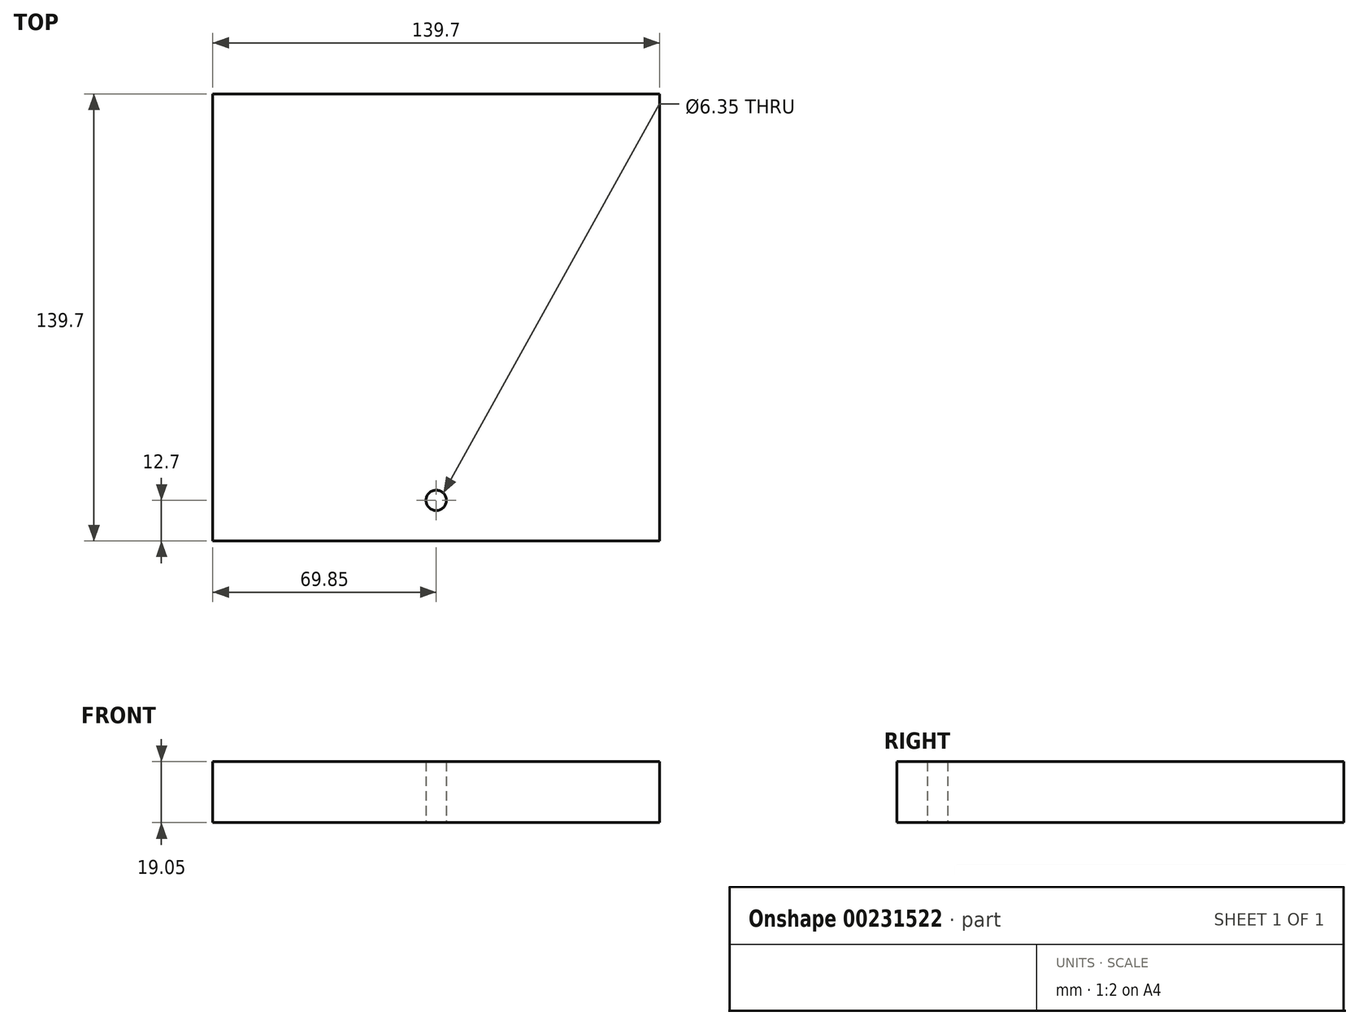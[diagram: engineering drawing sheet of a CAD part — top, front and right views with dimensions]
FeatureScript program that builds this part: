
annotation { "Feature Type Name" : "Feature", "Feature Type Description" : "" }
export const myFeature = defineFeature(function(context is Context, id is Id, definition is map)
    precondition{}
    {
        {
            var Q0;
            Q0=qCreatedBy(makeId("Top.planeOp"),FACE);
            var sketch = newSketch(context, id + "F0", { "sketchPlane" : qUnion([Q0])});
            skLineSegment(sketch, "E0.bottom", {"start": v(69.85, -69.85) * mm, "end": v(-69.85, -69.85) * mm});
            skLineSegment(sketch, "E0.top", {"start": v(69.85, 69.85) * mm, "end": v(-69.85, 69.85) * mm});
            skLineSegment(sketch, "E0.left", {"start": v(69.85, -69.85) * mm, "end": v(69.85, 69.85) * mm});
            skLineSegment(sketch, "E0.right", {"start": v(-69.85, -69.85) * mm, "end": v(-69.85, 69.85) * mm});
            skPoint(sketch, "E0.middle", {"position": v(0, 0) * mm});
            skLineSegment(sketch, "E1", {"start": v(0, -69.85) * mm, "end": v(0, -57.15) * mm});
            skCircle(sketch, "E2", {"center": v(0, -57.15) * mm, "radius": 3.18 * mm});
            skSolve(sketch);
        }
        {
            var Q0;
            Q0 = qSketchRegion(id + "F0", true);
            extrude(context, id + "F1", {"entities" : qUnion([Q0]), "depth" : 19.05 * mm});
        }
    });
